# Revit family: 14300-presto
name_source: partatom
category: Plumbing Fixtures
units: mm (PartAtom-declared; Revit-internal decimal feet)

## family parameters
Always vertical = Yes
Cut with Voids When Loaded = No
Maintain Annotation Orientation = No
OmniClass Number = 23.45.00.00
OmniClass Title = Sanitary, Laundry, and Cleaning Equipment
Part Type = Normal
Room Calculation Point = No
Round Connector Dimension = Use Diameter
Shared = No
Work Plane-Based = Yes

## types (1)
- 14300-presto
    Default Elevation = 1219 mm
    Description = 1000 XL E DVA - 3L/6L with brushed chrome-plated front plate
    Manufacturer = presto
    Model = 14300
    Recommended pressure = 3 bar
    URL = https://www.prestodatashare.com
    flow = 12.0 L/min
    flow time = 15.0 s
    min flow = 6.0 L/min
    min pressure = 1 bar
    ref = 14300 - PRESTO 1000 XL E DVA - 3L/6L with brushed chrome-plated front plate

## geometry (parser evidence)
native form markers: Sweep x2
no freeform markers — native parametric forms only
